# Revit family: HVAC_Heaters_Enertech_CTC-EcoVent-i360F
name_source: partatom
category: Specialty Equipment
revit_build: Autodesk Revit 2017 (Build: 20190508_0315(x64)
units: mm (PartAtom-declared; Revit-internal decimal feet)

## family parameters
Always vertical = Yes
Cut with Voids When Loaded = No
OmniClass Number = 23.75.00.00
OmniClass Title = Climate Control (HVAC)
Part Type = Normal
Room Calculation Point = No
Round Connector Dimension = Use Diameter
Shared = No
Work Plane-Based = No

## types (1)
- CTC EcoVent i360F - 400V3N
    AirFlow = 28 - 80 l/s
    AssetType = Fixed
    BIMObjectName = HVAC_Heaters_Enertech_CTC-EcoVent-i360F
    Brand = CTC
    Category = Ventilation solutions
    Color = white
    ConvergoRefNr = 0091-1710-0015-SE
    Cost = 0 $
    Description = The CTC EcoVent i360F is an indoor module with heat pump control and integrated ventilation, which, when used in combination with an air-to-water heat pump, makes the system significantly more energy-efficient, smarter and quieter. With the compressor located outside the building, you get a considerably quieter indoor climate. Since we use outdoor air to heat both the building and DHW you achieve better heating economy.
    DurationUnit = Year
    ElectricalDeviceNominalPower = 11900 W
    EnergyClass_HotWater_TapProfile = A / XL
    GroupFuse = 19
    HasProtectiveEarth = Yes
    HotTapWaterPerformance = 210 - 304 liters
    IP_Code = IP X1
    IfcExportAs = IfcElectricalDeviceCommon
    IfcExportType = HEATER
    Manufacturer = Enertech AB
    ManufacturerCountry = Sweden
    ManufacturerName = Enertech AB
    ManufacturerURL = https://ctc.se
    Material = Steel/copper
    MaxAirFlowRate = 80 l/s
    Model = CTC EcoVent i360F - 400V3N
    ModelNumber = 589700001
    NBSDescription = Air to water heat pumps
    NBSReference = 90-40-40/320
    Name = CTC-EcoVent-i360F
    NominalCurrent = 0 A
    NominalDepth = 673 mm  [stored 2.20801 ft]
    NominalFrequencyRange = 50 Hz
    NominalHeight = 2223 mm
    NominalVoltage = 400 V
    NominalWidth = 596 mm  [stored 1.95538 ft]
    NumberOfPoles = 3
    OutputRangeIimmersionHeater = 0.5-11.9 kW
    PhaseAngle = 0.00°
    PowerFactor = 0 W
    ProductInformation = The CTC EcoVent i360F is an indoor module with heat pump control and integrated ventilation, which, when used in combination with an air-to-water heat pump, makes the system significantly more energy-efficient, smarter and quieter. With the compressor located outside the building, you get a considerably quieter indoor climate. Since we use outdoor air to heat both the building and DHW you achieve better heating economy.
    PumpMainMaterial = Stainless Steel
    PumpSecondaryMaterial = Plastic, Opaque Black
    PumpTertiaryMaterial = Copper
    RatedCurrent = 19 A
    RatedHeatOutputModerate = 12 kW
    RatedVoltage = 1200 V
    ReferenceAirFlowRate = 56 l/s
    Shape = Rectangular
    Size = 673x596x2223 mm
    SoundPowerLWA = 45 dB
    URL = https://ctc-heating.com
    Uniclass2 = Pr_40_70_65
    Uniclass2015Description = Preparation catering equipment
    Uniclass2015Reference = Pr_40_70_65
    UsageCurrent = 0 A
    Version = 1
    VersionDate = 09/12/2020
    WarrantyDurationUnit = Year
    Weight = 184 kg

note: [stored X ft] marks values corroborated as IEEE doubles in the binary element streams (Revit-internal decimal feet)

## geometry (parser evidence)
native form markers: Sweep x7
no freeform markers — native parametric forms only
